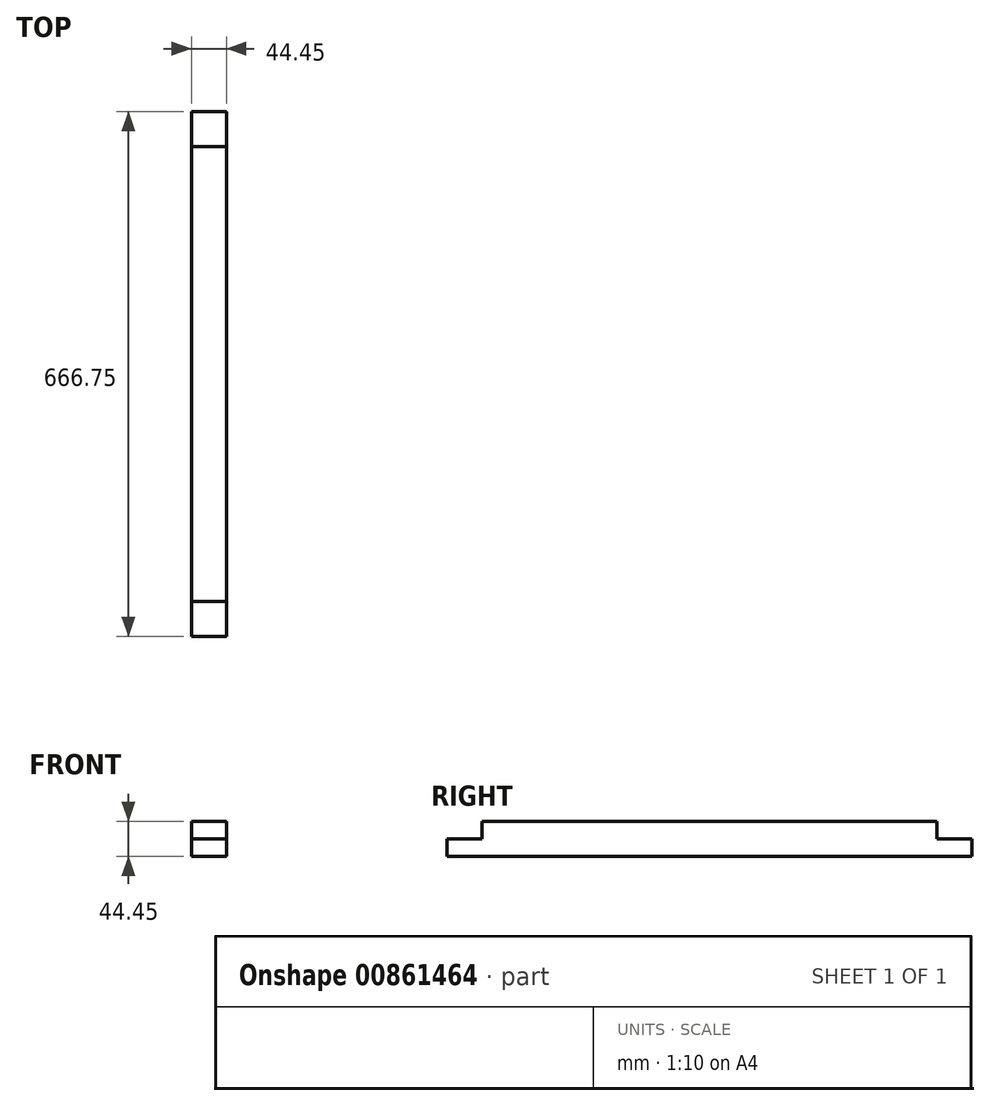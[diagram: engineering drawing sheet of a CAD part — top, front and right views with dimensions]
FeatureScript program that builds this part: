
annotation { "Feature Type Name" : "Feature", "Feature Type Description" : "" }
export const myFeature = defineFeature(function(context is Context, id is Id, definition is map)
    precondition{}
    {
        {
            var Q0;
            Q0=qCreatedBy(makeId("Front.planeOp"),FACE);
            var sketch = newSketch(context, id + "F0", { "sketchPlane" : qUnion([Q0])});
            skLineSegment(sketch, "E0.bottom", {"start": v(0, 0) * mm, "end": v(44.45, 0) * mm});
            skLineSegment(sketch, "E0.top", {"start": v(0, 44.45) * mm, "end": v(44.45, 44.45) * mm});
            skLineSegment(sketch, "E0.left", {"start": v(0, 0) * mm, "end": v(0, 44.45) * mm});
            skLineSegment(sketch, "E0.right", {"start": v(44.45, 0) * mm, "end": v(44.45, 44.45) * mm});
            skSolve(sketch);
        }
        {
            var Q0;
            Q0=makeQuery(id+"F0.imprint","IMPRINT",FACE,{"disambiguationData":[TD([[makeQuery(id+"F0.imprint","IMPRINT",EDGE,{"derivedFrom":sQuery(id+"F0.wireOp",EDGE,"E0.bottom")}),1.0]])]});
            extrude(context, id + "F1", {"entities" : qUnion([Q0]), "depth" : 666.75 * mm, "offsetDistance" : 25.4 * mm});
        }
        {
            var Q0;
            Q0=makeQuery(id+"F1.opExtrude","SWEPT_FACE",FACE,{"disambiguationData":[OSD([sQuery(id+"F0.wireOp",EDGE,"E0.top")])]});
            var sketch = newSketch(context, id + "F2", { "sketchPlane" : qUnion([Q0])});
            skLineSegment(sketch, "E1.bottom", {"start": v(0, -666.75) * mm, "end": v(44.45, -666.75) * mm});
            skLineSegment(sketch, "E1.top", {"start": v(0, -622.3) * mm, "end": v(44.45, -622.3) * mm});
            skLineSegment(sketch, "E1.left", {"start": v(0, -666.75) * mm, "end": v(0, -622.3) * mm});
            skLineSegment(sketch, "E1.right", {"start": v(44.45, -666.75) * mm, "end": v(44.45, -622.3) * mm});
            skLineSegment(sketch, "E2.bottom", {"start": v(0, 0) * mm, "end": v(44.45, 0) * mm});
            skLineSegment(sketch, "E2.top", {"start": v(0, -44.45) * mm, "end": v(44.45, -44.45) * mm});
            skLineSegment(sketch, "E2.left", {"start": v(0, 0) * mm, "end": v(0, -44.45) * mm});
            skLineSegment(sketch, "E2.right", {"start": v(44.45, 0) * mm, "end": v(44.45, -44.45) * mm});
            skSolve(sketch);
        }
        {
            var Q0;
            Q0=qSketchRegion(id+"F2",true);
            extrude(context, id + "F3", {"entities" : qUnion([Q0]), "operationType" : NewBodyOperationType.REMOVE, "oppositeDirection" : true, "depth" : 22.22 * mm, "offsetDistance" : 25.4 * mm});
        }
    });
